# Revit family: Plumbing-Faucet-Sloan-Valve-SF-2400z
name_source: partatom
category: Plumbing Fixtures
units: mm (PartAtom-declared; Revit-internal decimal feet)

## family parameters
Cut with Voids When Loaded = No
Host = Face
OmniClass Number = 23.45.55.14
OmniClass Title = Single Faucets
Part Type = Normal
Room Calculation Point = No
Round Connector Dimension = Use Diameter
Shared = No

## types (3) — shared parameters
Apparent Load = 0 VA
Assembly Code = D2010
CW Connection = Yes
CWFU = 1.5
Current = 0 A
Default Elevation = 0"
Depth = 5 3/4"
Edition number = 1
HW Connection = Yes
HWFU = 1.5
Height = 5"
Keynote = 15410
Manufacturer = Sloan Valve
Number of Poles = 3
Power Factor = 0.8
Pretempered Water Connection Diameter = 0"
Product Material = Sloan Valve - Finish - Polished Chrome
Product data url = https://bimobject.com
URL = www.sloanvalve.com
Valve Pressure Drop = 0.00 psi
Vent Connection = No
Voltage = 6 V
Waste Connection = No
Width = 6 1/4"
z_No Trim Plate = No
z_Trim Plate 4 = Yes
z_Trim Plate 8 = No
z_Trim Plate Length = 6 1/8"
zero-valued in all types: WFU

## per-type parameters (varying)
| type | Description | Part Number | Water Flow |
| SF-2400-4-PLG-BDM-CP-0.5GPM-MLM-IR-FCT | 4" Trim Plate, Plug Adapter Power Supply, Below Deck Manual Mixing Valve, Polished Chrome Finish, 0.5 gpm, Multi-Laminar Spray, Infrared Sensor, Sloan® Hardwired-Powered Deck-Mounted Mid Body Faucet. | 3362133 | 1 GPM |
| SF-2400-4-PLG-TEE-CP-0.35GPM-MLM-IR-FCT | 4" Trim Plate, Plug Adapter Power Supply, Back-Check Tee, Polished Chrome Finish, 0.35 gpm, Multi-Laminar Spray, Infrared Sensor, Sloan® Hardwired-Powered Deck-Mounted Mid Body Faucet. | 3362178 | 0 GPM |
| SF-2400-4-PLG-TEE-CP-0.5GPM-MLM-IR-FCT | 4" Trim Plate, Plug Adapter Power Supply, Back-Check Tee, Polished Chrome Finish, 0.5 gpm, Multi-Laminar Spray, Infrared Sensor, Sloan® Hardwired-Powered Deck-Mounted Mid Body Faucet. | 3362130 | 1 GPM |

note: column(s) folded — value = type name in every type: Model

## geometry (parser evidence)
native form markers: Sweep x6
no freeform markers — native parametric forms only
